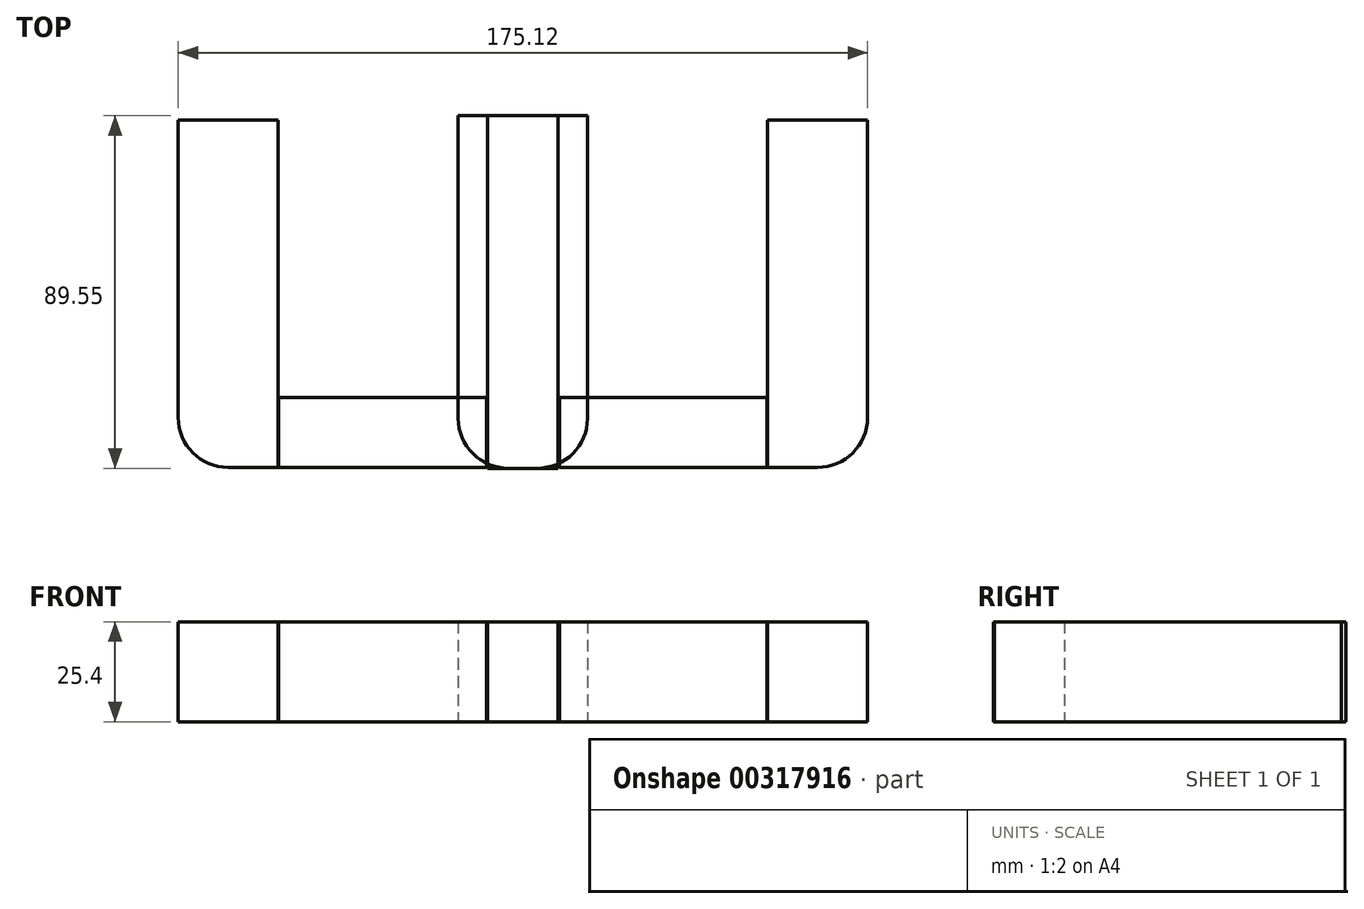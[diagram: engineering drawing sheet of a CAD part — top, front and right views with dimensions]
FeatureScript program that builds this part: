
annotation { "Feature Type Name" : "Feature", "Feature Type Description" : "" }
export const myFeature = defineFeature(function(context is Context, id is Id, definition is map)
    precondition{}
    {
        {
            var Q0;
            Q0=qCreatedBy(makeId("Top.planeOp"),FACE);
            var sketch = newSketch(context, id + "F0", { "sketchPlane" : qUnion([Q0])});
            skLineSegment(sketch, "E0.bottom", {"start": v(-16.43, 36.46) * mm, "end": v(8.97, 36.46) * mm});
            skLineSegment(sketch, "E0.top", {"start": v(-3.73, -53.09) * mm, "end": v(8.97, -53.09) * mm});
            skLineSegment(sketch, "E0.left", {"start": v(-16.43, 36.46) * mm, "end": v(-16.43, -40.39) * mm});
            skLineSegment(sketch, "E0.right", {"start": v(8.97, 36.46) * mm, "end": v(8.97, -53.09) * mm});
            skLineSegment(sketch, "E1.bottom", {"start": v(9.27, -35.1) * mm, "end": v(62.04, -35.1) * mm});
            skLineSegment(sketch, "E1.top", {"start": v(9.27, -52.88) * mm, "end": v(62.04, -52.88) * mm});
            skLineSegment(sketch, "E1.left", {"start": v(9.27, -35.1) * mm, "end": v(9.27, -52.88) * mm});
            skLineSegment(sketch, "E1.right", {"start": v(62.04, -35.1) * mm, "end": v(62.04, -52.88) * mm});
            skLineSegment(sketch, "E2.left", {"start": v(62.04, -35.1) * mm, "end": v(62.1, -35.17) * mm});
            skLineSegment(sketch, "E3.bottom", {"start": v(62.16, -52.88) * mm, "end": v(74.86, -52.88) * mm});
            skLineSegment(sketch, "E3.top", {"start": v(62.16, 35.32) * mm, "end": v(87.56, 35.32) * mm});
            skLineSegment(sketch, "E3.left", {"start": v(62.16, -52.88) * mm, "end": v(62.16, 35.32) * mm});
            skLineSegment(sketch, "E3.right", {"start": v(87.56, -40.18) * mm, "end": v(87.56, 35.32) * mm});
            skPoint(sketch, "E4.visualSharp", {"position": v(87.56, -52.88) * mm});
            skArc(sketch, "E4.filletArc", {"start": v(74.86, -52.88) * mm, "mid": v(83.84, -49.16) * mm, "end": v(87.56, -40.18) * mm});
            skPoint(sketch, "E5.visualSharp", {"position": v(-16.43, -53.09) * mm});
            skArc(sketch, "E5.filletArc", {"start": v(-16.43, -40.39) * mm, "mid": v(-12.7, -49.37) * mm, "end": v(-3.73, -53.09) * mm});
            skSolve(sketch);
        }
        {
            var Q0;
            Q0 = qSketchRegion(id + "F0", true);
            extrude(context, id + "F1", {"entities" : qUnion([Q0]), "depth" : 25.4 * mm});
        }
        {
            var Q0;
            Q0=makeQuery(id+"F1.opExtrude","SWEPT_BODY",BODY,{"disambiguationData":[OSD([sQuery(id+"F0.wireOp",EDGE,"E0.bottom"),sQuery(id+"F0.wireOp",EDGE,"E0.top"),sQuery(id+"F0.wireOp",EDGE,"E0.left"),sQuery(id+"F0.wireOp",EDGE,"E0.right"),sQuery(id+"F0.wireOp",EDGE,"E5.filletArc")])]});
            var Q1;
            Q1=makeQuery(id+"F1.opExtrude","SWEPT_BODY",BODY,{"disambiguationData":[OSD([sQuery(id+"F0.wireOp",EDGE,"E1.bottom"),sQuery(id+"F0.wireOp",EDGE,"E1.top"),sQuery(id+"F0.wireOp",EDGE,"E1.left"),sQuery(id+"F0.wireOp",EDGE,"E1.right")])]});
            var Q2;
            Q2=makeQuery(id+"F1.opExtrude","SWEPT_BODY",BODY,{"disambiguationData":[OSD([sQuery(id+"F0.wireOp",EDGE,"E3.bottom"),sQuery(id+"F0.wireOp",EDGE,"E3.top"),sQuery(id+"F0.wireOp",EDGE,"E3.left"),sQuery(id+"F0.wireOp",EDGE,"E3.right"),sQuery(id+"F0.wireOp",EDGE,"E4.filletArc")])]});
            var Q3;
            Q3=qCreatedBy(makeId("Right.planeOp"),FACE);
            mirror(context, id + "F2", {"entities" : qUnion([Q0, Q1, Q2]), "mirrorPlane" : qUnion([Q3])});
        }
    });
